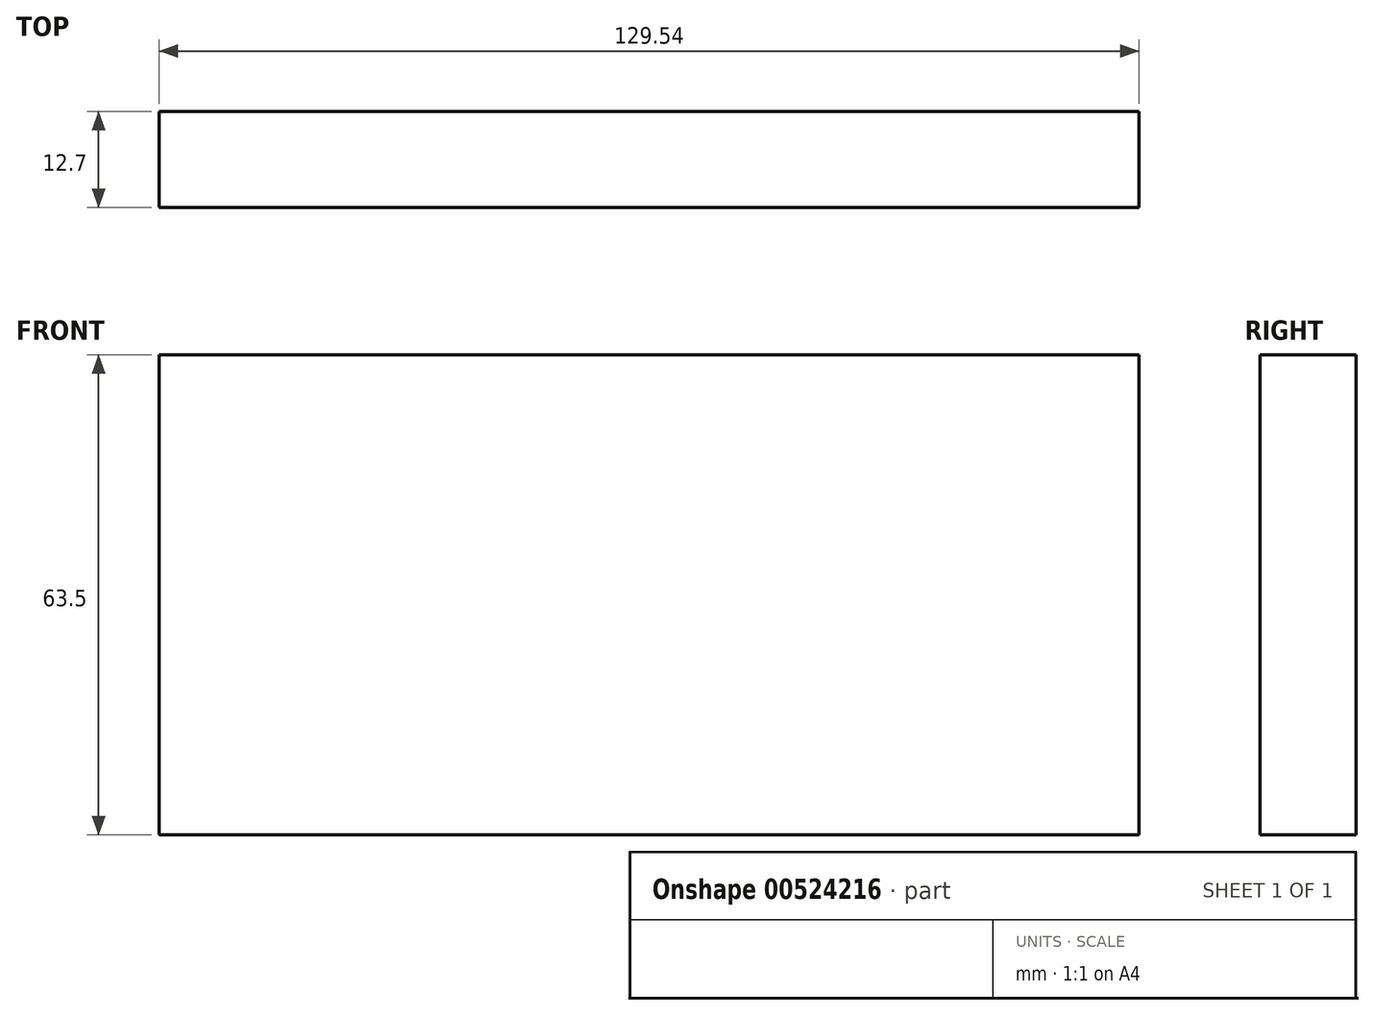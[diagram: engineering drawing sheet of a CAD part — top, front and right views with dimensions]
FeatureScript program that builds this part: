
annotation { "Feature Type Name" : "Feature", "Feature Type Description" : "" }
export const myFeature = defineFeature(function(context is Context, id is Id, definition is map)
    precondition{}
    {
        {
            var Q0;
            Q0=qCreatedBy(makeId("Front.planeOp"),FACE);
            var sketch = newSketch(context, id + "F0", { "sketchPlane" : qUnion([Q0])});
            skLineSegment(sketch, "E0.bottom", {"start": v(-64.77, 31.75) * mm, "end": v(64.77, 31.75) * mm});
            skLineSegment(sketch, "E0.top", {"start": v(-64.77, -31.75) * mm, "end": v(64.77, -31.75) * mm});
            skLineSegment(sketch, "E0.left", {"start": v(-64.77, 31.75) * mm, "end": v(-64.77, -31.75) * mm});
            skLineSegment(sketch, "E0.right", {"start": v(64.77, 31.75) * mm, "end": v(64.77, -31.75) * mm});
            skSolve(sketch);
        }
        {
            var Q0;
            Q0 = qSketchRegion(id + "F0", true);
            extrude(context, id + "F1", {"entities" : qUnion([Q0]), "endBound" : BoundingType.SYMMETRIC, "depth" : 12.7 * mm, "offsetDistance" : 25.4 * mm});
        }
    });
